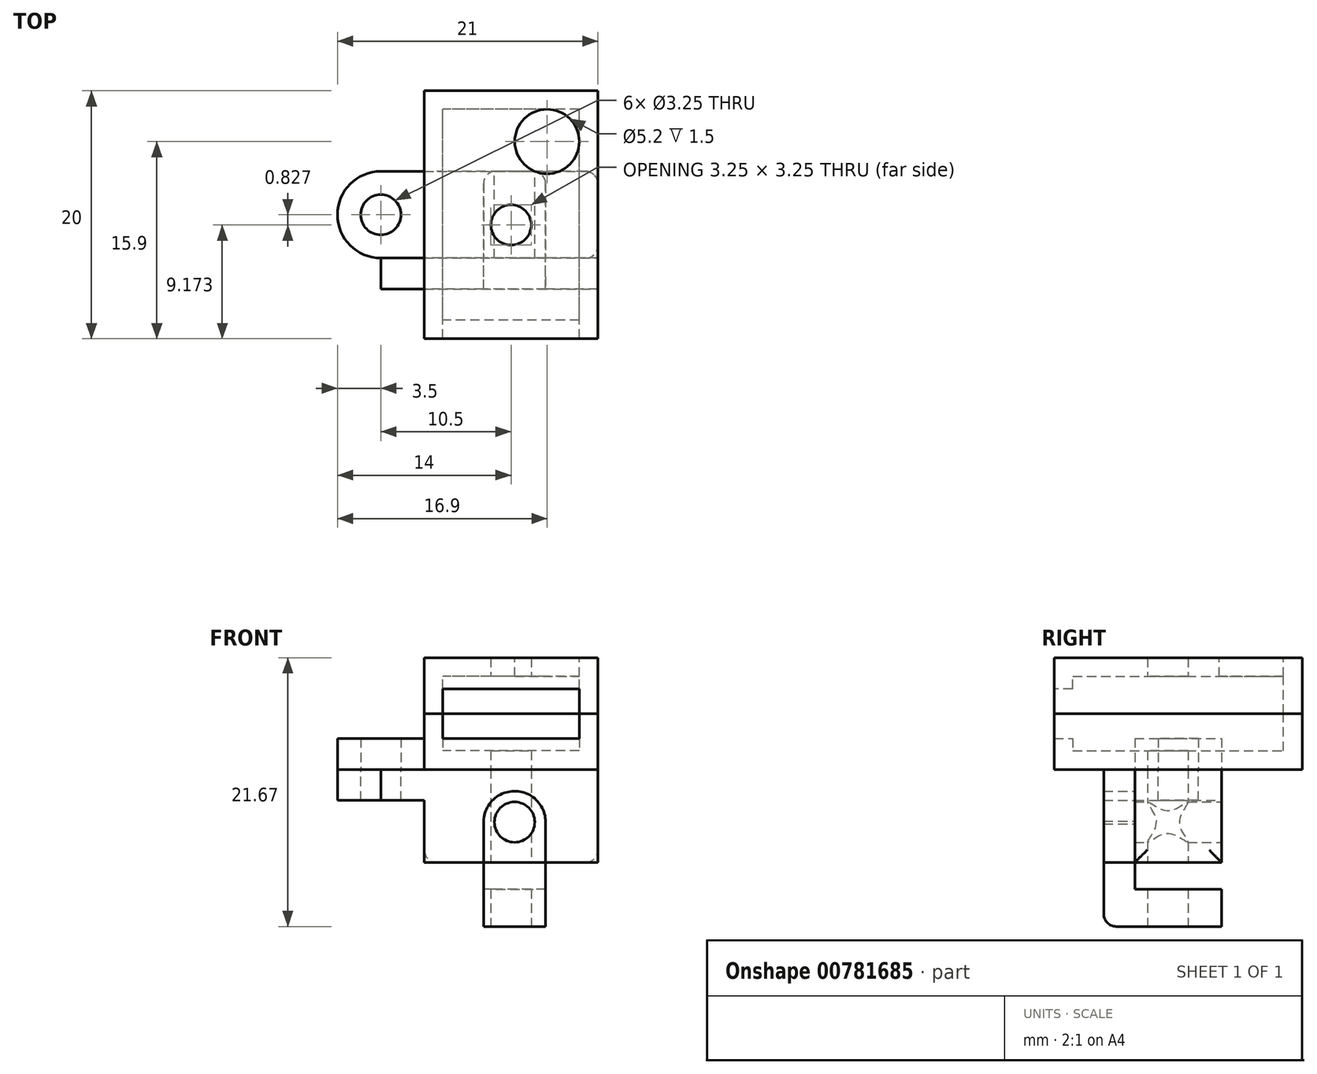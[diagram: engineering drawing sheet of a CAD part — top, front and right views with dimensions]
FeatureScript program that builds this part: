
annotation { "Feature Type Name" : "Feature", "Feature Type Description" : "" }
export const myFeature = defineFeature(function(context is Context, id is Id, definition is map)
    precondition{}
    {
        {
            var Q0;
            Q0=qCreatedBy(makeId("Top.planeOp"),FACE);
            var sketch = newSketch(context, id + "F0", { "sketchPlane" : qUnion([Q0])});
            skLineSegment(sketch, "E0.bottom", {"start": v(5.5, -8.5) * mm, "end": v(-5.5, -8.5) * mm});
            skLineSegment(sketch, "E0.top", {"start": v(5.5, 8.5) * mm, "end": v(-5.5, 8.5) * mm});
            skLineSegment(sketch, "E0.left", {"start": v(5.5, -8.5) * mm, "end": v(5.5, 8.5) * mm});
            skLineSegment(sketch, "E0.right", {"start": v(-5.5, -8.5) * mm, "end": v(-5.5, 8.5) * mm});
            skPoint(sketch, "E0.middle", {"position": v(0, 0) * mm});
            skLineSegment(sketch, "E1.bottom", {"start": v(-7, -10) * mm, "end": v(7, -10) * mm});
            skLineSegment(sketch, "E1.top", {"start": v(-7, 10) * mm, "end": v(7, 10) * mm});
            skLineSegment(sketch, "E1.left", {"start": v(-7, -10) * mm, "end": v(-7, 10) * mm});
            skLineSegment(sketch, "E1.right", {"start": v(7, -10) * mm, "end": v(7, 10) * mm});
            skSolve(sketch);
        }
        {
            var Q0;
            Q0=makeQuery(id+"F0.imprint","IMPRINT",FACE,{"disambiguationData":[TD([[makeQuery(id+"F0.imprint","IMPRINT",EDGE,{"derivedFrom":sQuery(id+"F0.wireOp",EDGE,"E0.bottom")}),-1.0]])]});
            extrude(context, id + "F1", {"entities" : qUnion([Q0]), "depth" : 1.5 * mm, "offsetDistance" : 25 * mm});
        }
        {
            var Q0;
            Q0=makeQuery(id+"F1.opExtrude","CAP_FACE",FACE,{"disambiguationData":[OSD([sQuery(id+"F0.wireOp",EDGE,"E0.bottom"),sQuery(id+"F0.wireOp",EDGE,"E0.top"),sQuery(id+"F0.wireOp",EDGE,"E0.left"),sQuery(id+"F0.wireOp",EDGE,"E0.right")])],"isStart":false});
            var sketch = newSketch(context, id + "F2", { "sketchPlane" : qUnion([Q0])});
            skLineSegment(sketch, "E2", {"start": v(5.5, 8.5) * mm, "end": v(2.9, 8.5) * mm, "construction": true});
            skLineSegment(sketch, "E3", {"start": v(2.9, 8.5) * mm, "end": v(2.9, 5.9) * mm, "construction": true});
            skCircle(sketch, "E4", {"center": v(2.9, 5.9) * mm, "radius": 2.6 * mm});
            skSolve(sketch);
        }
        {
            var Q0;
            {var subQ0=sQuery(id+"F2.wireOp",EDGE,"E4");var subQ1=makeQuery(id+"F2.imprint","INTERSECT",VERTEX,{"derivedFrom":[makeQuery(id+"F1.opExtrude","CAP_EDGE",EDGE,{"disambiguationData":[OSD([sQuery(id+"F0.wireOp",EDGE,"E0.top")])],"isStart":false}),subQ0]});Q0=makeQuery(id+"F2.imprint","IMPRINT",FACE,{"disambiguationData":[TD([[makeQuery(id+"F2.imprint","IMPRINT",EDGE,{"disambiguationData":[TD([[subQ1,1.0]])],"derivedFrom":subQ0}),1.0]])]});}
            extrude(context, id + "F3", {"entities" : qUnion([Q0]), "operationType" : NewBodyOperationType.REMOVE, "oppositeDirection" : true, "depth" : 25 * mm, "offsetDistance" : 25 * mm});
        }
        {
            var Q0;
            Q0=makeQuery(id+"F0.imprint","IMPRINT",FACE,{"disambiguationData":[TD([[makeQuery(id+"F0.imprint","IMPRINT",EDGE,{"derivedFrom":sQuery(id+"F0.wireOp",EDGE,"E0.bottom")}),1.0]])]});
            var Q1;
            {var subQ0=sQuery(id+"F0.wireOp",EDGE,"E0.left");var subQ1=sQuery(id+"F0.wireOp",EDGE,"E0.top");var subQ2=sQuery(id+"F0.wireOp",EDGE,"E0.right");var subQ3=sQuery(id+"F0.wireOp",EDGE,"E0.bottom");Q1=makeQuery(id+"F3.boolean.opBoolean","SPLIT",FACE,{"disambiguationData":[TD([makeQuery(id+"F1.opExtrude","SWEPT_FACE",FACE,{"disambiguationData":[OSD([subQ3])]}),makeQuery(id+"F1.opExtrude","SWEPT_FACE",FACE,{"disambiguationData":[OSD([subQ1])]}),makeQuery(id+"F1.opExtrude","SWEPT_FACE",FACE,{"disambiguationData":[OSD([subQ0])]}),makeQuery(id+"F1.opExtrude","SWEPT_FACE",FACE,{"disambiguationData":[OSD([subQ2])]}),makeQuery(id+"F3.opExtrude","SWEPT_FACE",FACE,{"disambiguationData":[OSD([sQuery(id+"F2.wireOp",EDGE,"E4")])]})])],"derivedFrom":makeQuery(id+"F1.opExtrude","CAP_FACE",FACE,{"disambiguationData":[OSD([subQ3,subQ1,subQ0,subQ2])],"isStart":false})});}
            extrude(context, id + "F4", {"entities" : qUnion([Q0]), "operationType" : NewBodyOperationType.ADD, "endBound" : BoundingType.UP_TO_SURFACE, "depth" : 3.5 * mm, "endBoundEntityFace" : qUnion([Q1]), "offsetDistance" : 25 * mm});
        }
        {
            var Q0;
            Q0=makeQuery(id+"F0.imprint","IMPRINT",FACE,{"disambiguationData":[TD([[makeQuery(id+"F0.imprint","IMPRINT",EDGE,{"derivedFrom":sQuery(id+"F0.wireOp",EDGE,"E0.bottom")}),1.0]])]});
            extrude(context, id + "F5", {"entities" : qUnion([Q0]), "operationType" : NewBodyOperationType.ADD, "oppositeDirection" : true, "depth" : 3 * mm, "offsetDistance" : 25 * mm});
        }
        {
            var Q0;
            Q0=makeQuery(id+"F5.opExtrude","CAP_FACE",FACE,{"disambiguationData":[OSD([sQuery(id+"F0.wireOp",EDGE,"E0.bottom"),sQuery(id+"F0.wireOp",EDGE,"E0.top"),sQuery(id+"F0.wireOp",EDGE,"E0.left"),sQuery(id+"F0.wireOp",EDGE,"E0.right"),sQuery(id+"F0.wireOp",EDGE,"E1.bottom"),sQuery(id+"F0.wireOp",EDGE,"E1.top"),sQuery(id+"F0.wireOp",EDGE,"E1.left"),sQuery(id+"F0.wireOp",EDGE,"E1.right")])],"isStart":false});
            var sketch = newSketch(context, id + "F6", { "sketchPlane" : qUnion([Q0])});
            skLineSegment(sketch, "E5", {"start": v(5.5, 8.5) * mm, "end": v(5.5, 10) * mm});
            skLineSegment(sketch, "E6", {"start": v(-5.5, 8.5) * mm, "end": v(-5.5, 10) * mm});
            skSolve(sketch);
        }
        {
            var Q0;
            {var subQ0=sQuery(id+"F6.wireOp",EDGE,"E5");Q0=makeQuery(id+"F6.imprint","IMPRINT",FACE,{"disambiguationData":[TD([[makeQuery(id+"F6.imprint","IMPRINT",EDGE,{"derivedFrom":subQ0}),1.0]])]});}
            extrude(context, id + "F7", {"entities" : qUnion([Q0]), "operationType" : NewBodyOperationType.REMOVE, "oppositeDirection" : true, "depth" : 2 * mm, "offsetDistance" : 25 * mm});
        }
        {
            var Q0;
            Q0=makeQuery(id+"F5.opExtrude","CAP_FACE",FACE,{"disambiguationData":[OSD([sQuery(id+"F0.wireOp",EDGE,"E0.bottom"),sQuery(id+"F0.wireOp",EDGE,"E0.top"),sQuery(id+"F0.wireOp",EDGE,"E0.left"),sQuery(id+"F0.wireOp",EDGE,"E0.right"),sQuery(id+"F0.wireOp",EDGE,"E1.bottom"),sQuery(id+"F0.wireOp",EDGE,"E1.top"),sQuery(id+"F0.wireOp",EDGE,"E1.left"),sQuery(id+"F0.wireOp",EDGE,"E1.right")])],"isStart":false});
            extrude(context, id + "F8", {"entities" : qUnion([Q0]), "depth" : 3 * mm, "offsetDistance" : 25 * mm});
        }
        {
            var Q0;
            Q0=makeQuery(id+"F8.opExtrude","CAP_FACE",FACE,{"disambiguationData":[OSD([sQuery(id+"F0.wireOp",EDGE,"E0.bottom"),sQuery(id+"F0.wireOp",EDGE,"E0.top"),sQuery(id+"F0.wireOp",EDGE,"E0.left"),sQuery(id+"F0.wireOp",EDGE,"E0.right"),sQuery(id+"F0.wireOp",EDGE,"E1.bottom"),sQuery(id+"F0.wireOp",EDGE,"E1.top"),sQuery(id+"F0.wireOp",EDGE,"E1.left"),sQuery(id+"F0.wireOp",EDGE,"E1.right")])],"isStart":false});
            var sketch = newSketch(context, id + "F9", { "sketchPlane" : qUnion([Q0])});
            skLineSegment(sketch, "E7", {"start": v(5.5, 10) * mm, "end": v(5.5, 8.5) * mm});
            skLineSegment(sketch, "E8", {"start": v(5.5, 8.5) * mm, "end": v(-5.5, 8.5) * mm});
            skLineSegment(sketch, "E9", {"start": v(-5.5, 8.5) * mm, "end": v(-5.5, 10) * mm});
            skLineSegment(sketch, "E10", {"start": v(-5.5, 10) * mm, "end": v(5.5, 10) * mm});
            skSolve(sketch);
        }
        {
            var Q0;
            Q0=makeQuery(id+"F9.imprint","IMPRINT",FACE,{"disambiguationData":[TD([[makeQuery(id+"F9.imprint","IMPRINT",EDGE,{"derivedFrom":sQuery(id+"F9.wireOp",EDGE,"E7")}),-1.0]])]});
            extrude(context, id + "F10", {"entities" : qUnion([Q0]), "operationType" : NewBodyOperationType.ADD, "oppositeDirection" : true, "depth" : 1 * mm, "offsetDistance" : 25 * mm});
        }
        {
            var Q0;
            Q0=makeQuery(id+"F8.opExtrude","SWEPT_FACE",FACE,{"disambiguationData":[OSD([sQuery(id+"F0.wireOp",EDGE,"E1.right")])]});
            var sketch = newSketch(context, id + "F11", { "sketchPlane" : qUnion([Q0])});
            skLineSegment(sketch, "E11", {"start": v(10, -6) * mm, "end": v(10, -7.5) * mm});
            skLineSegment(sketch, "E12", {"start": v(10, -7.5) * mm, "end": v(-10, -7.5) * mm});
            skLineSegment(sketch, "E13", {"start": v(-10, -7.5) * mm, "end": v(-10, -6) * mm});
            skSolve(sketch);
        }
        {
            var Q0;
            Q0=makeQuery(id+"F11.imprint","IMPRINT",FACE,{"disambiguationData":[TD([[makeQuery(id+"F11.imprint","IMPRINT",EDGE,{"derivedFrom":sQuery(id+"F11.wireOp",EDGE,"E11")}),-1.0]])]});
            var Q1;
            Q1=makeQuery(id+"F8.opExtrude","SWEPT_FACE",FACE,{"disambiguationData":[OSD([sQuery(id+"F0.wireOp",EDGE,"E1.left")])]});
            extrude(context, id + "F12", {"entities" : qUnion([Q0]), "operationType" : NewBodyOperationType.ADD, "endBound" : BoundingType.UP_TO_SURFACE, "oppositeDirection" : true, "depth" : 25 * mm, "endBoundEntityFace" : qUnion([Q1]), "offsetDistance" : 25 * mm});
        }
        {
            var Q0;
            Q0=makeQuery(id+"F12.opExtrude","SWEPT_FACE",FACE,{"disambiguationData":[OSD([sQuery(id+"F11.wireOp",EDGE,"E12")])]});
            var sketch = newSketch(context, id + "F13", { "sketchPlane" : qUnion([Q0])});
            skLineSegment(sketch, "E14", {"start": v(-7, 0) * mm, "end": v(-10.5, 0) * mm, "construction": true});
            skCircle(sketch, "E15", {"center": v(-10.5, 0) * mm, "radius": 1.63 * mm});
            skCircle(sketch, "E16", {"center": v(-10.5, 0) * mm, "radius": 3.5 * mm});
            skLineSegment(sketch, "E17", {"start": v(-10.5, 0) * mm, "end": v(-10.5, 3.5) * mm, "construction": true});
            skLineSegment(sketch, "E18", {"start": v(-10.5, 3.5) * mm, "end": v(-7, 3.5) * mm});
            skLineSegment(sketch, "E19", {"start": v(-10.5, 0) * mm, "end": v(-10.5, -3.5) * mm, "construction": true});
            skLineSegment(sketch, "E20", {"start": v(-10.5, -3.5) * mm, "end": v(-7, -3.5) * mm});
            skSolve(sketch);
        }
        {
            var Q0;
            {var subQ0=sQuery(id+"F13.wireOp",EDGE,"E18");Q0=makeQuery(id+"F13.imprint","IMPRINT",FACE,{"disambiguationData":[TD([[makeQuery(id+"F13.imprint","IMPRINT",EDGE,{"derivedFrom":subQ0}),-1.0]])]});}
            var Q1;
            Q1=makeQuery(id+"F13.imprint","IMPRINT",FACE,{"disambiguationData":[TD([[makeQuery(id+"F13.imprint","IMPRINT",EDGE,{"derivedFrom":sQuery(id+"F13.wireOp",EDGE,"E15")}),-1.0]])]});
            var Q2;
            {var subQ0=sQuery(id+"F13.wireOp",EDGE,"E20");Q2=makeQuery(id+"F13.imprint","IMPRINT",FACE,{"disambiguationData":[TD([[makeQuery(id+"F13.imprint","IMPRINT",EDGE,{"derivedFrom":subQ0}),1.0]])]});}
            extrude(context, id + "F14", {"entities" : qUnion([Q0, Q1, Q2]), "operationType" : NewBodyOperationType.ADD, "oppositeDirection" : true, "depth" : 2.5 * mm, "offsetDistance" : 25 * mm});
        }
        {
            var Q0;
            {var subQ0=sQuery(id+"F11.wireOp",EDGE,"E12");Q0=makeQuery(id+"F14.boolean.opBoolean","MERGE",FACE,{"derivedFrom":[makeQuery(id+"F12.opExtrude","SWEPT_FACE",FACE,{"disambiguationData":[OSD([subQ0])]}),makeQuery(id+"F14.opExtrude","CAP_FACE",FACE,{"disambiguationData":[OSD([sQuery(id+"F0.wireOp",EDGE,"E1.left"),subQ0,sQuery(id+"F13.wireOp",EDGE,"E15"),sQuery(id+"F13.wireOp",EDGE,"E16"),sQuery(id+"F13.wireOp",EDGE,"E18"),sQuery(id+"F13.wireOp",EDGE,"E20")])],"isStart":true})]});}
            var sketch = newSketch(context, id + "F15", { "sketchPlane" : qUnion([Q0])});
            skCircle(sketch, "E21", {"center": v(-10.5, 0) * mm, "radius": 1.6 * mm});
            skCircle(sketch, "E22", {"center": v(-10.5, 0) * mm, "radius": 3.5 * mm});
            skLineSegment(sketch, "E23", {"start": v(-10.5, 3.5) * mm, "end": v(7, 3.5) * mm});
            skLineSegment(sketch, "E24", {"start": v(7, 3.5) * mm, "end": v(7, -3.5) * mm});
            skLineSegment(sketch, "E25", {"start": v(7, -3.5) * mm, "end": v(-10.5, -3.5) * mm});
            skSolve(sketch);
        }
        {
            var Q0;
            {var subQ0=sQuery(id+"F15.wireOp",EDGE,"E24");Q0=makeQuery(id+"F15.imprint","IMPRINT",FACE,{"disambiguationData":[TD([[makeQuery(id+"F15.imprint","IMPRINT",EDGE,{"derivedFrom":subQ0}),1.0]])]});}
            var Q1;
            Q1=makeQuery(id+"F15.imprint","IMPRINT",FACE,{"disambiguationData":[TD([[makeQuery(id+"F15.imprint","IMPRINT",EDGE,{"derivedFrom":makeQuery(id+"F14.opExtrude","CAP_EDGE",EDGE,{"disambiguationData":[OSD([sQuery(id+"F13.wireOp",EDGE,"E15")])],"isStart":true})}),-1.0]])]});
            extrude(context, id + "F16", {"entities" : qUnion([Q0, Q1]), "depth" : 2.5 * mm, "offsetDistance" : 25 * mm});
        }
        {
            var Q0;
            Q0=makeQuery(id+"F16.opExtrude","SWEPT_FACE",FACE,{"disambiguationData":[OSD([sQuery(id+"F15.wireOp",EDGE,"E25")])]});
            var sketch = newSketch(context, id + "F17", { "sketchPlane" : qUnion([Q0])});
            skLineSegment(sketch, "E26", {"start": v(-0.28, -10) * mm, "end": v(-0.28, -13.5) * mm});
            skCircle(sketch, "E27", {"center": v(-0.28, -11.75) * mm, "radius": 1.63 * mm});
            skLineSegment(sketch, "E28", {"start": v(-0.28, -10) * mm, "end": v(-7, -10) * mm});
            skLineSegment(sketch, "E29", {"start": v(-7, -10) * mm, "end": v(-7, -15) * mm});
            skLineSegment(sketch, "E30", {"start": v(-7, -15) * mm, "end": v(7, -15) * mm});
            skLineSegment(sketch, "E31", {"start": v(7, -15) * mm, "end": v(7, -10) * mm});
            skSolve(sketch);
        }
        {
            var Q0;
            {var subQ0=sQuery(id+"F17.wireOp",EDGE,"E28");Q0=makeQuery(id+"F17.imprint","IMPRINT",FACE,{"disambiguationData":[TD([[makeQuery(id+"F17.imprint","IMPRINT",EDGE,{"derivedFrom":subQ0}),1.0]])]});}
            var Q1;
            Q1=makeQuery(id+"F16.opExtrude","SWEPT_FACE",FACE,{"disambiguationData":[OSD([sQuery(id+"F15.wireOp",EDGE,"E23")])]});
            extrude(context, id + "F18", {"entities" : qUnion([Q0]), "operationType" : NewBodyOperationType.ADD, "endBound" : BoundingType.UP_TO_SURFACE, "oppositeDirection" : true, "depth" : 25 * mm, "endBoundEntityFace" : qUnion([Q1]), "offsetDistance" : 25 * mm});
        }
        {
            var Q0;
            {var subQ0=sQuery(id+"F15.wireOp",EDGE,"E23");Q0=makeQuery(id+"F18.boolean.opBoolean","MERGE",FACE,{"derivedFrom":[makeQuery(id+"F16.opExtrude","SWEPT_FACE",FACE,{"disambiguationData":[OSD([subQ0])]}),makeQuery(id+"F18.opExtrude","CAP_FACE",FACE,{"disambiguationData":[OSD([subQ0])],"isStart":false})]});}
            var sketch = newSketch(context, id + "F19", { "sketchPlane" : qUnion([Q0])});
            skCircle(sketch, "E32", {"center": v(0.28, -11.75) * mm, "radius": 1.6 * mm});
            skCircle(sketch, "E33", {"center": v(0.28, -11.75) * mm, "radius": 2.5 * mm});
            skLineSegment(sketch, "E34", {"start": v(-2.21, -11.67) * mm, "end": v(-2.21, -17.67) * mm});
            skLineSegment(sketch, "E35", {"start": v(-2.21, -17.67) * mm, "end": v(2.78, -17.67) * mm});
            skLineSegment(sketch, "E36", {"start": v(2.78, -17.67) * mm, "end": v(2.78, -11.61) * mm});
            skSolve(sketch);
        }
        {
            var Q0;
            {var subQ0=sQuery(id+"F19.wireOp",EDGE,"E35");Q0=makeQuery(id+"F19.imprint","IMPRINT",FACE,{"disambiguationData":[TD([[makeQuery(id+"F19.imprint","IMPRINT",EDGE,{"derivedFrom":subQ0}),1.0]])]});}
            var Q1;
            {var subQ0=sQuery(id+"F19.wireOp",EDGE,"E34");var subQ1=sQuery(id+"F19.wireOp",EDGE,"E33");var subQ2=makeQuery(id+"F19.imprint","INTERSECT",VERTEX,{"disambiguationData":[OD(1.0)],"derivedFrom":[subQ1,subQ0]});Q1=makeQuery(id+"F19.imprint","IMPRINT",FACE,{"disambiguationData":[TD([[makeQuery(id+"F19.imprint","IMPRINT",EDGE,{"disambiguationData":[TD([[subQ2,-1.0]])],"derivedFrom":subQ1}),-1.0]])]});}
            var Q2;
            {var subQ0=sQuery(id+"F19.wireOp",EDGE,"E34");var subQ1=sQuery(id+"F19.wireOp",EDGE,"E33");var subQ2=makeQuery(id+"F19.imprint","INTERSECT",VERTEX,{"disambiguationData":[OD(0.0)],"derivedFrom":[subQ1,subQ0]});Q2=makeQuery(id+"F19.imprint","IMPRINT",FACE,{"disambiguationData":[TD([[makeQuery(id+"F19.imprint","IMPRINT",EDGE,{"disambiguationData":[TD([[subQ2,1.0]])],"derivedFrom":subQ1}),1.0]])]});}
            extrude(context, id + "F20", {"entities" : qUnion([Q0, Q1, Q2]), "depth" : 2.5 * mm, "offsetDistance" : 25 * mm});
        }
        {
            var Q0;
            Q0=makeQuery(id+"F20.opExtrude","CAP_FACE",FACE,{"disambiguationData":[OSD([sQuery(id+"F15.wireOp",EDGE,"E23"),sQuery(id+"F17.wireOp",EDGE,"E27"),sQuery(id+"F19.wireOp",EDGE,"E33"),sQuery(id+"F19.wireOp",EDGE,"E34"),sQuery(id+"F19.wireOp",EDGE,"E35"),sQuery(id+"F19.wireOp",EDGE,"E36")])],"isStart":true});
            var sketch = newSketch(context, id + "F21", { "sketchPlane" : qUnion([Q0])});
            skLineSegment(sketch, "E37", {"start": v(-2.78, -17.67) * mm, "end": v(-2.78, -15.67) * mm});
            skLineSegment(sketch, "E38", {"start": v(-2.78, -15.67) * mm, "end": v(2.21, -15.67) * mm});
            skLineSegment(sketch, "E39", {"start": v(2.21, -15.67) * mm, "end": v(2.21, -17.67) * mm});
            skLineSegment(sketch, "E40", {"start": v(2.21, -17.67) * mm, "end": v(-2.78, -17.67) * mm});
            skSolve(sketch);
        }
        {
            var Q0;
            Q0=makeQuery(id+"F21.imprint","IMPRINT",FACE,{"disambiguationData":[TD([[makeQuery(id+"F21.imprint","IMPRINT",EDGE,{"derivedFrom":sQuery(id+"F21.wireOp",EDGE,"E37")}),-1.0]])]});
            var Q1;
            {var subQ0=sQuery(id+"F15.wireOp",EDGE,"E25");Q1=makeQuery(id+"F18.boolean.opBoolean","MERGE",FACE,{"derivedFrom":[makeQuery(id+"F16.opExtrude","SWEPT_FACE",FACE,{"disambiguationData":[OSD([subQ0])]}),makeQuery(id+"F18.opExtrude","CAP_FACE",FACE,{"disambiguationData":[OSD([subQ0,sQuery(id+"F17.wireOp",EDGE,"E27"),sQuery(id+"F17.wireOp",EDGE,"E28"),sQuery(id+"F17.wireOp",EDGE,"E29"),sQuery(id+"F17.wireOp",EDGE,"E30"),sQuery(id+"F17.wireOp",EDGE,"E31")])],"isStart":true})]});}
            extrude(context, id + "F22", {"entities" : qUnion([Q0]), "operationType" : NewBodyOperationType.ADD, "endBound" : BoundingType.UP_TO_SURFACE, "depth" : 25 * mm, "endBoundEntityFace" : qUnion([Q1]), "offsetDistance" : 25 * mm});
        }
        {
            var Q0;
            Q0=makeQuery(id+"F22.opExtrude","SWEPT_FACE",FACE,{"disambiguationData":[OSD([sQuery(id+"F21.wireOp",EDGE,"E38")])]});
            extrude(context, id + "F23", {"entities" : qUnion([Q0]), "operationType" : NewBodyOperationType.REMOVE, "oppositeDirection" : true, "depth" : 1.5 * mm, "offsetDistance" : 25 * mm});
        }
        {
            var Q0;
            Q0=makeQuery(id+"F22.boolean.opBoolean","MERGE",FACE,{"derivedFrom":[makeQuery(id+"F20.opExtrude","SWEPT_FACE",FACE,{"disambiguationData":[OSD([sQuery(id+"F19.wireOp",EDGE,"E35")])]}),makeQuery(id+"F22.opExtrude","SWEPT_FACE",FACE,{"disambiguationData":[OSD([sQuery(id+"F21.wireOp",EDGE,"E40")])]})]});
            extrude(context, id + "F24", {"entities" : qUnion([Q0]), "operationType" : NewBodyOperationType.ADD, "depth" : 2.5 * mm, "offsetDistance" : 25 * mm});
        }
        {
            var Q0;
            Q0=makeQuery(id+"F24.opExtrude","CAP_FACE",FACE,{"disambiguationData":[OSD([sQuery(id+"F19.wireOp",EDGE,"E35"),sQuery(id+"F21.wireOp",EDGE,"E40")])],"isStart":false});
            var sketch = newSketch(context, id + "F25", { "sketchPlane" : qUnion([Q0])});
            skCircle(sketch, "E41", {"center": v(0, 0.83) * mm, "radius": 1.63 * mm});
            skSolve(sketch);
        }
        {
            var Q0;
            Q0=makeQuery(id+"F25.imprint","IMPRINT",FACE,{"disambiguationData":[TD([[makeQuery(id+"F25.imprint","IMPRINT",EDGE,{"derivedFrom":sQuery(id+"F25.wireOp",EDGE,"E41")}),1.0]])]});
            extrude(context, id + "F26", {"entities" : qUnion([Q0]), "operationType" : NewBodyOperationType.REMOVE, "oppositeDirection" : true, "depth" : 25 * mm, "offsetDistance" : 25 * mm});
        }
        {
            var Q0;
            {var subQ0=sQuery(id+"F21.wireOp",EDGE,"E39");var subQ1=sQuery(id+"F17.wireOp",EDGE,"E31");var subQ2=sQuery(id+"F17.wireOp",EDGE,"E30");var subQ3=sQuery(id+"F17.wireOp",EDGE,"E29");var subQ4=sQuery(id+"F17.wireOp",EDGE,"E28");var subQ5=sQuery(id+"F17.wireOp",EDGE,"E27");var subQ6=sQuery(id+"F15.wireOp",EDGE,"E25");Q0=makeQuery(id+"F24.boolean.opBoolean","MERGE",EDGE,{"derivedFrom":[makeQuery(id+"F22.opExtrude","TWEAK_EDGE",EDGE,{"derivedFrom":[makeQuery(id+"F18.boolean.opBoolean","MERGE",FACE,{"derivedFrom":[makeQuery(id+"F16.opExtrude","SWEPT_FACE",FACE,{"disambiguationData":[OSD([subQ6])]}),makeQuery(id+"F18.opExtrude","CAP_FACE",FACE,{"disambiguationData":[OSD([subQ6,subQ5,subQ4,subQ3,subQ2,subQ1])],"isStart":true})]}),makeQuery(id+"F21.imprint","IMPRINT",EDGE,{"derivedFrom":subQ0})]}),makeQuery(id+"F24.opExtrude","SWEPT_EDGE",EDGE,{"disambiguationData":[OSD([subQ6,subQ5,subQ4,subQ3,subQ2,subQ1,subQ0,sQuery(id+"F21.wireOp",EDGE,"E40")])]})]});}
            var Q1;
            Q1=makeQuery(id+"F24.opExtrude","CAP_EDGE",EDGE,{"disambiguationData":[OSD([sQuery(id+"F19.wireOp",EDGE,"E35")])],"isStart":false});
            var Q2;
            {var subQ0=sQuery(id+"F21.wireOp",EDGE,"E37");var subQ1=sQuery(id+"F17.wireOp",EDGE,"E31");var subQ2=sQuery(id+"F17.wireOp",EDGE,"E30");var subQ3=sQuery(id+"F17.wireOp",EDGE,"E29");var subQ4=sQuery(id+"F17.wireOp",EDGE,"E28");var subQ5=sQuery(id+"F17.wireOp",EDGE,"E27");var subQ6=sQuery(id+"F15.wireOp",EDGE,"E25");Q2=makeQuery(id+"F24.boolean.opBoolean","MERGE",EDGE,{"derivedFrom":[makeQuery(id+"F22.opExtrude","TWEAK_EDGE",EDGE,{"derivedFrom":[makeQuery(id+"F18.boolean.opBoolean","MERGE",FACE,{"derivedFrom":[makeQuery(id+"F16.opExtrude","SWEPT_FACE",FACE,{"disambiguationData":[OSD([subQ6])]}),makeQuery(id+"F18.opExtrude","CAP_FACE",FACE,{"disambiguationData":[OSD([subQ6,subQ5,subQ4,subQ3,subQ2,subQ1])],"isStart":true})]}),makeQuery(id+"F21.imprint","IMPRINT",EDGE,{"derivedFrom":subQ0})]}),makeQuery(id+"F24.opExtrude","SWEPT_EDGE",EDGE,{"disambiguationData":[OSD([subQ6,subQ5,subQ4,subQ3,subQ2,subQ1,subQ0,sQuery(id+"F21.wireOp",EDGE,"E40")])]})]});}
            var Q3;
            Q3=makeQuery(id+"F18.opExtrude","SWEPT_EDGE",EDGE,{"disambiguationData":[OSD([sQuery(id+"F17.wireOp",EDGE,"E30"),sQuery(id+"F17.wireOp",EDGE,"E31")])]});
            var Q4;
            Q4=makeQuery(id+"F18.opExtrude","SWEPT_EDGE",EDGE,{"disambiguationData":[OSD([sQuery(id+"F17.wireOp",EDGE,"E29"),sQuery(id+"F17.wireOp",EDGE,"E30")])]});
            var Q5;
            Q5=makeQuery(id+"F18.boolean.opBoolean","MERGE",EDGE,{"derivedFrom":[makeQuery(id+"F16.opExtrude","SWEPT_EDGE",EDGE,{"disambiguationData":[OSD([sQuery(id+"F11.wireOp",EDGE,"E12"),sQuery(id+"F15.wireOp",EDGE,"E24"),sQuery(id+"F15.wireOp",EDGE,"E25")])]}),makeQuery(id+"F18.opExtrude","CAP_EDGE",EDGE,{"disambiguationData":[OSD([sQuery(id+"F17.wireOp",EDGE,"E29")])],"isStart":true})]});
            var Q6;
            {var subQ0=sQuery(id+"F15.wireOp",EDGE,"E23");Q6=makeQuery(id+"F18.boolean.opBoolean","MERGE",EDGE,{"derivedFrom":[makeQuery(id+"F16.opExtrude","SWEPT_EDGE",EDGE,{"disambiguationData":[OSD([sQuery(id+"F11.wireOp",EDGE,"E12"),subQ0,sQuery(id+"F15.wireOp",EDGE,"E24")])]}),makeQuery(id+"F18.opExtrude","TWEAK_EDGE",EDGE,{"derivedFrom":[makeQuery(id+"F16.opExtrude","SWEPT_FACE",FACE,{"disambiguationData":[OSD([subQ0])]}),makeQuery(id+"F17.imprint","IMPRINT",EDGE,{"derivedFrom":sQuery(id+"F17.wireOp",EDGE,"E29")})]})]});}
            fillet(context, id + "F27", {"entities" : qUnion([Q0, Q1, Q2, Q3, Q4, Q5, Q6]), "radius" : 1 * mm, "tangentPropagation" : true, "allowEdgeOverflow" : false});
        }
    });
